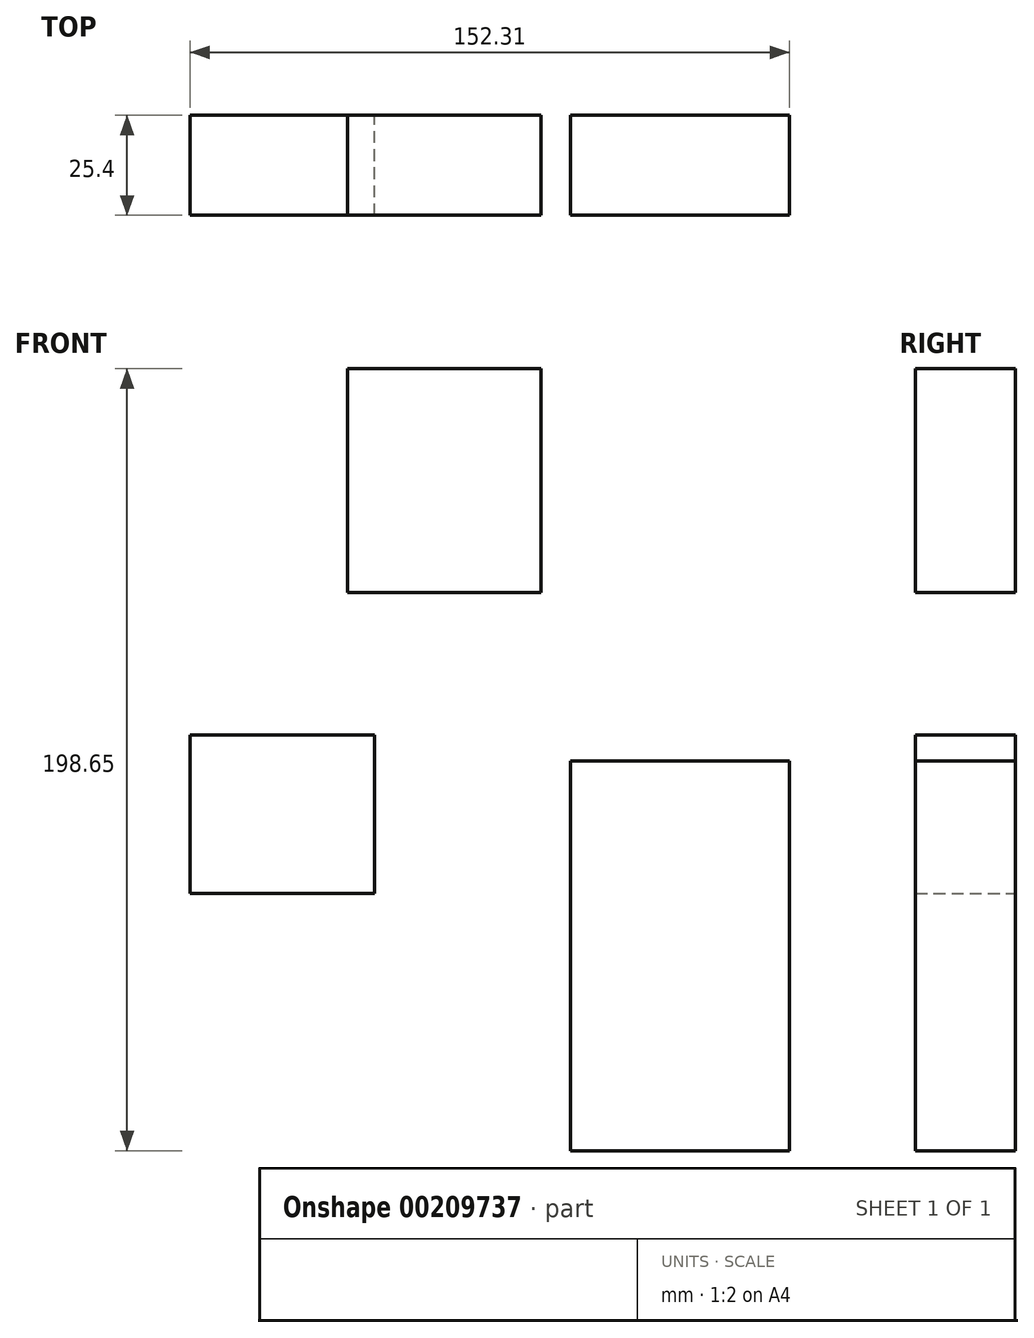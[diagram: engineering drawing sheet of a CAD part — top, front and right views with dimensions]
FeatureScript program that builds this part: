
annotation { "Feature Type Name" : "Feature", "Feature Type Description" : "" }
export const myFeature = defineFeature(function(context is Context, id is Id, definition is map)
    precondition{}
    {
        {
            var Q0;
            Q0=qCreatedBy(makeId("Front.planeOp"),FACE);
            var sketch = newSketch(context, id + "F0", { "sketchPlane" : qUnion([Q0])});
            skLineSegment(sketch, "E0.bottom", {"start": v(-7.3, 155.41) * mm, "end": v(41.88, 155.41) * mm});
            skLineSegment(sketch, "E0.top", {"start": v(-7.3, 98.56) * mm, "end": v(41.88, 98.56) * mm});
            skLineSegment(sketch, "E0.left", {"start": v(-7.3, 155.41) * mm, "end": v(-7.3, 98.56) * mm});
            skLineSegment(sketch, "E0.right", {"start": v(41.88, 155.41) * mm, "end": v(41.88, 98.56) * mm});
            skLineSegment(sketch, "E1.bottom", {"start": v(-47.3, 62.4) * mm, "end": v(-0.42, 62.4) * mm});
            skLineSegment(sketch, "E1.top", {"start": v(-47.3, 22.17) * mm, "end": v(-0.42, 22.17) * mm});
            skLineSegment(sketch, "E1.left", {"start": v(-47.3, 62.4) * mm, "end": v(-47.3, 22.17) * mm});
            skLineSegment(sketch, "E1.right", {"start": v(-0.42, 62.4) * mm, "end": v(-0.42, 22.17) * mm});
            skLineSegment(sketch, "E2.bottom", {"start": v(49.38, 55.72) * mm, "end": v(105.01, 55.72) * mm});
            skLineSegment(sketch, "E2.top", {"start": v(49.38, -43.24) * mm, "end": v(105.01, -43.24) * mm});
            skLineSegment(sketch, "E2.left", {"start": v(49.38, 55.72) * mm, "end": v(49.38, -43.24) * mm});
            skLineSegment(sketch, "E2.right", {"start": v(105.01, 55.72) * mm, "end": v(105.01, -43.24) * mm});
            skSolve(sketch);
        }
        {
            var Q0;
            Q0=makeQuery(id+"F0.imprint","IMPRINT",FACE,{"disambiguationData":[TD([[makeQuery(id+"F0.imprint","IMPRINT",EDGE,{"derivedFrom":sQuery(id+"F0.wireOp",EDGE,"E1.bottom")}),-1.0]])]});
            var Q1;
            Q1=makeQuery(id+"F0.imprint","IMPRINT",FACE,{"disambiguationData":[TD([[makeQuery(id+"F0.imprint","IMPRINT",EDGE,{"derivedFrom":sQuery(id+"F0.wireOp",EDGE,"E0.bottom")}),-1.0]])]});
            var Q2;
            Q2=makeQuery(id+"F0.imprint","IMPRINT",FACE,{"disambiguationData":[TD([[makeQuery(id+"F0.imprint","IMPRINT",EDGE,{"derivedFrom":sQuery(id+"F0.wireOp",EDGE,"E2.bottom")}),-1.0]])]});
            extrude(context, id + "F1", {"entities" : qUnion([Q0, Q1, Q2]), "depth" : 25.4 * mm});
        }
    });
